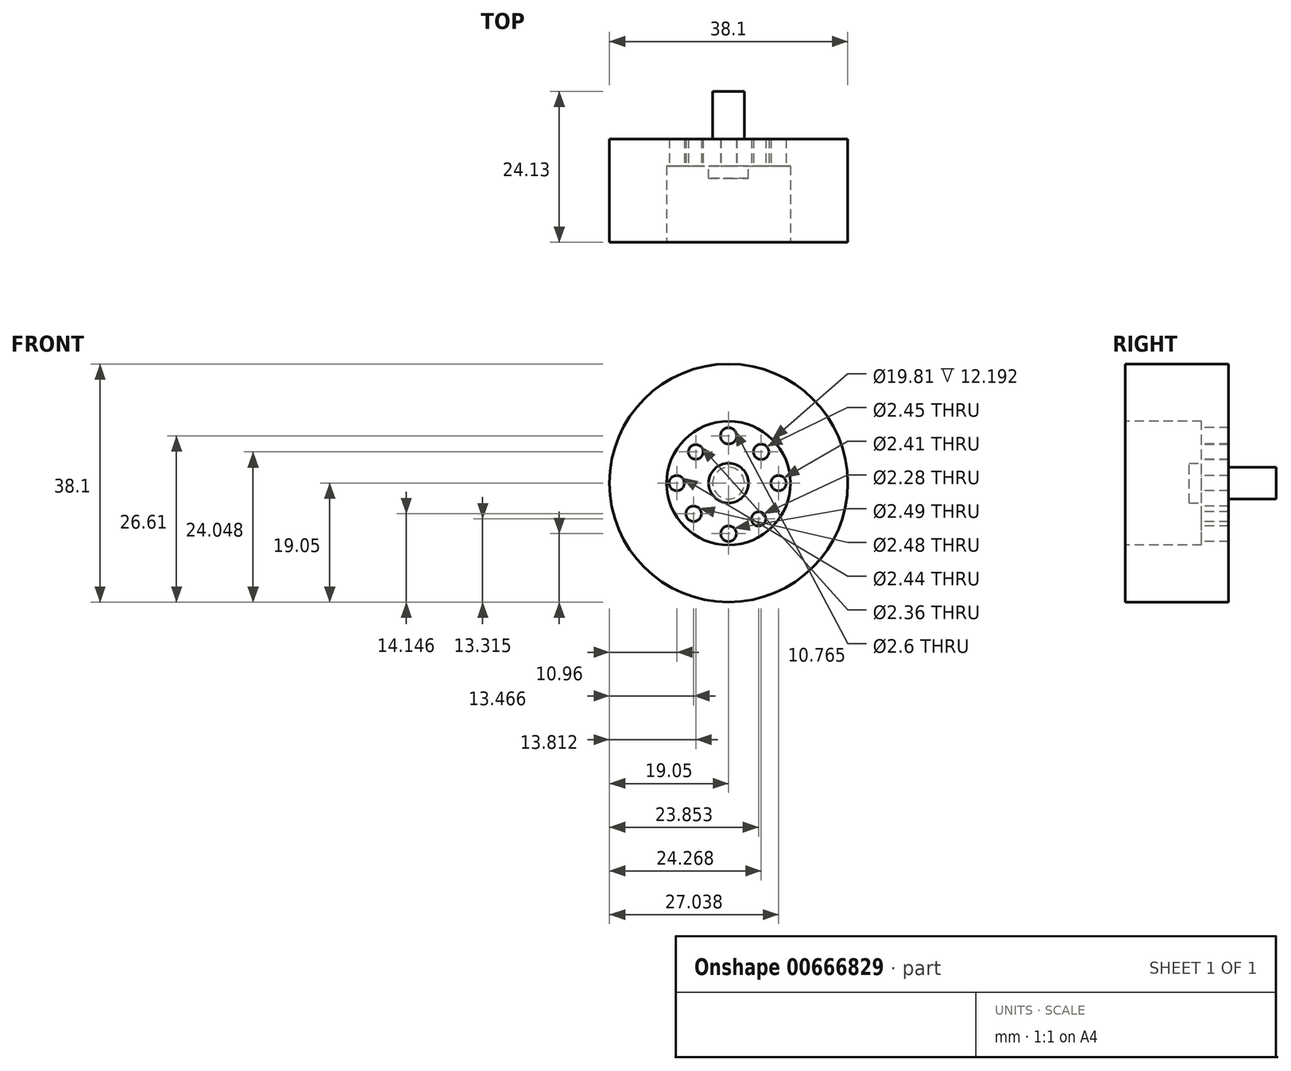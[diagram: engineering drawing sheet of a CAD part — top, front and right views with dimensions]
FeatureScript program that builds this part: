
annotation { "Feature Type Name" : "Feature", "Feature Type Description" : "" }
export const myFeature = defineFeature(function(context is Context, id is Id, definition is map)
    precondition{}
    {
        {
            var Q0;
            Q0=qCreatedBy(makeId("Front.planeOp"),FACE);
            var sketch = newSketch(context, id + "F0", { "sketchPlane" : qUnion([Q0])});
            skCircle(sketch, "E0", {"center": v(0, 0) * mm, "radius": 19.05 * mm});
            skSolve(sketch);
        }
        {
            var Q0;
            Q0 = qSketchRegion(id + "F0", true);
            extrude(context, id + "F1", {"entities" : qUnion([Q0]), "depth" : 16.5 * mm, "offsetDistance" : 25.4 * mm});
        }
        {
            var Q0;
            Q0=makeQuery(id+"F1.opExtrude","CAP_FACE",FACE,{"disambiguationData":[OSD([sQuery(id+"F0.wireOp",EDGE,"E0")])],"isStart":false});
            var sketch = newSketch(context, id + "F2", { "sketchPlane" : qUnion([Q0])});
            skCircle(sketch, "E1", {"center": v(0, 0) * mm, "radius": 9.9 * mm});
            skSolve(sketch);
        }
        {
            var Q0;
            Q0=makeQuery(id+"F2.imprint","IMPRINT",FACE,{"disambiguationData":[TD([[makeQuery(id+"F2.imprint","IMPRINT",EDGE,{"derivedFrom":sQuery(id+"F2.wireOp",EDGE,"E1")}),1.0]])]});
            extrude(context, id + "F3", {"entities" : qUnion([Q0]), "operationType" : NewBodyOperationType.REMOVE, "oppositeDirection" : true, "depth" : 12.2 * mm, "offsetDistance" : 25.4 * mm});
        }
        {
            var Q0;
            Q0=makeQuery(id+"F3.boolean.opBoolean","COPY",FACE,{"derivedFrom":makeQuery(id+"F3.opExtrude","CAP_FACE",FACE,{"disambiguationData":[OSD([sQuery(id+"F2.wireOp",EDGE,"E1")])],"isStart":false})});
            var sketch = newSketch(context, id + "F4", { "sketchPlane" : qUnion([Q0])});
            skCircle(sketch, "E2", {"center": v(0, 0) * mm, "radius": 3.18 * mm});
            skSolve(sketch);
        }
        {
            var Q0;
            Q0=makeQuery(id+"F4.imprint","IMPRINT",FACE,{"disambiguationData":[TD([[makeQuery(id+"F4.imprint","IMPRINT",EDGE,{"derivedFrom":sQuery(id+"F4.wireOp",EDGE,"E2")}),1.0]])]});
            extrude(context, id + "F5", {"entities" : qUnion([Q0]), "operationType" : NewBodyOperationType.ADD, "depth" : 2 * mm, "offsetDistance" : 25.4 * mm});
        }
        {
            var Q0;
            Q0=makeQuery(id+"F3.boolean.opBoolean","COPY",FACE,{"derivedFrom":makeQuery(id+"F3.opExtrude","CAP_FACE",FACE,{"disambiguationData":[OSD([sQuery(id+"F2.wireOp",EDGE,"E1")])],"isStart":false})});
            var sketch = newSketch(context, id + "F6", { "sketchPlane" : qUnion([Q0])});
            skCircle(sketch, "E3", {"center": v(0, 7.56) * mm, "radius": 1.3 * mm});
            skCircle(sketch, "E4", {"center": v(-8.28, 0) * mm, "radius": 1.22 * mm});
            skCircle(sketch, "E5", {"center": v(7.99, 0) * mm, "radius": 1.2 * mm});
            skCircle(sketch, "E6", {"center": v(0, -8.09) * mm, "radius": 1.24 * mm});
            skCircle(sketch, "E7", {"center": v(5.22, 5) * mm, "radius": 1.23 * mm});
            skCircle(sketch, "E8", {"center": v(4.8, -5.74) * mm, "radius": 1.14 * mm});
            skCircle(sketch, "E9", {"center": v(-5.58, -4.9) * mm, "radius": 1.24 * mm});
            skCircle(sketch, "E10", {"center": v(-5.24, 5) * mm, "radius": 1.18 * mm});
            skSolve(sketch);
        }
        {
            var Q0;
            Q0=makeQuery(id+"F6.imprint","IMPRINT",FACE,{"disambiguationData":[TD([[makeQuery(id+"F6.imprint","IMPRINT",EDGE,{"derivedFrom":sQuery(id+"F6.wireOp",EDGE,"E3")}),1.0]])]});
            var Q1;
            Q1=makeQuery(id+"F6.imprint","IMPRINT",FACE,{"disambiguationData":[TD([[makeQuery(id+"F6.imprint","IMPRINT",EDGE,{"derivedFrom":sQuery(id+"F6.wireOp",EDGE,"E10")}),1.0]])]});
            var Q2;
            Q2=makeQuery(id+"F6.imprint","IMPRINT",FACE,{"disambiguationData":[TD([[makeQuery(id+"F6.imprint","IMPRINT",EDGE,{"derivedFrom":sQuery(id+"F6.wireOp",EDGE,"E4")}),1.0]])]});
            var Q3;
            Q3=makeQuery(id+"F6.imprint","IMPRINT",FACE,{"disambiguationData":[TD([[makeQuery(id+"F6.imprint","IMPRINT",EDGE,{"derivedFrom":sQuery(id+"F6.wireOp",EDGE,"E9")}),1.0]])]});
            var Q4;
            Q4=makeQuery(id+"F6.imprint","IMPRINT",FACE,{"disambiguationData":[TD([[makeQuery(id+"F6.imprint","IMPRINT",EDGE,{"derivedFrom":sQuery(id+"F6.wireOp",EDGE,"E6")}),1.0]])]});
            var Q5;
            Q5=makeQuery(id+"F6.imprint","IMPRINT",FACE,{"disambiguationData":[TD([[makeQuery(id+"F6.imprint","IMPRINT",EDGE,{"derivedFrom":sQuery(id+"F6.wireOp",EDGE,"E8")}),1.0]])]});
            var Q6;
            Q6=makeQuery(id+"F6.imprint","IMPRINT",FACE,{"disambiguationData":[TD([[makeQuery(id+"F6.imprint","IMPRINT",EDGE,{"derivedFrom":sQuery(id+"F6.wireOp",EDGE,"E5")}),1.0]])]});
            var Q7;
            Q7=makeQuery(id+"F6.imprint","IMPRINT",FACE,{"disambiguationData":[TD([[makeQuery(id+"F6.imprint","IMPRINT",EDGE,{"derivedFrom":sQuery(id+"F6.wireOp",EDGE,"E7")}),1.0]])]});
            extrude(context, id + "F7", {"entities" : qUnion([Q0, Q1, Q2, Q3, Q4, Q5, Q6, Q7]), "operationType" : NewBodyOperationType.REMOVE, "oppositeDirection" : true, "depth" : 25.4 * mm, "offsetDistance" : 25.4 * mm});
        }
        {
            var Q0;
            Q0=makeQuery(id+"F1.opExtrude","CAP_FACE",FACE,{"disambiguationData":[OSD([sQuery(id+"F0.wireOp",EDGE,"E0")])],"isStart":true});
            var sketch = newSketch(context, id + "F8", { "sketchPlane" : qUnion([Q0])});
            skCircle(sketch, "E11", {"center": v(0, 0) * mm, "radius": 2.54 * mm});
            skSolve(sketch);
        }
        {
            var Q0;
            Q0=makeQuery(id+"F8.imprint","IMPRINT",FACE,{"disambiguationData":[TD([[makeQuery(id+"F8.imprint","IMPRINT",EDGE,{"derivedFrom":sQuery(id+"F8.wireOp",EDGE,"E11")}),1.0]])]});
            extrude(context, id + "F9", {"entities" : qUnion([Q0]), "operationType" : NewBodyOperationType.ADD, "depth" : 7.62 * mm, "offsetDistance" : 25.4 * mm});
        }
    });
